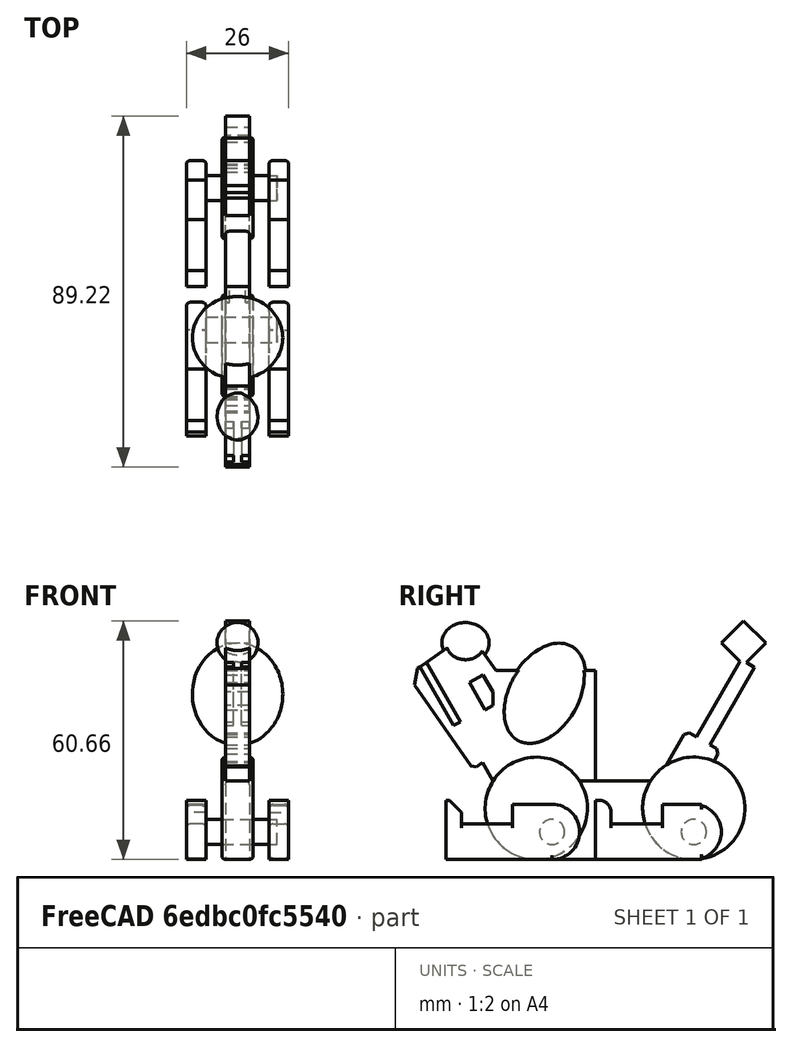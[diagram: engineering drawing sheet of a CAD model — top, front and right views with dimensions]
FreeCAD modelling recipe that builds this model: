
FCSTD DOCUMENT  (FreeCAD 0.18R16117 (Git))
Label: Robo puppy
License: All rights reserved
LicenseURL: http://en.wikipedia.org/wiki/All_rights_reserved
objects: Part::Box×16, Part::Fillet×10, Part::Cylinder×8, Part::MultiFuse×6, Part::Cut×5, Part::Chamfer×4, Part::Mirroring×2, Part::Ellipsoid×2, Part::Plane×1
note: 54 computed .brp shape members not serialized (recipe doc carries the construction recipe); baked Part::Feature solids carry a one-line shape summary decoded from their .brp

FEATURE [Part::Plane] Plane
  AttacherType = Attacher::AttachEngine3D
  Length = 100
  Placement = pos=(-50,-50,0) rot=(0,0,1;0rad)
  Width = 100
FEATURE [Part::Box] Box  label="Cube"
  AttacherType = Attacher::AttachEngine3D
  Height = 20
  Length = 6
  Placement = pos=(-3,-20,0) rot=(0,0,1;0rad)
  Width = 40
FEATURE [Part::Cylinder] Cylinder  label="wheel1"
  Angle = 360
  AttacherType = Attacher::AttachEngine3D
  Height = 8
  Placement = pos=(-4,-20,13) rot=(0,1,0;1.5708rad)
  Radius = 13
FEATURE [Part::Cylinder] Cylinder001  label="wheel2"
  Angle = 360
  AttacherType = Attacher::AttachEngine3D
  Height = 8
  Placement = pos=(-4,20,13) rot=(0,1,0;1.5708rad)
  Radius = 13
FEATURE [Part::Cylinder] Cylinder002  label="wheel003"
  Angle = 360
  AttacherType = Attacher::AttachEngine3D
  Height = 18
  Placement = pos=(-8,-16,7) rot=(0,1,0;1.5708rad)
  Radius = 3.2
FEATURE [Part::Cylinder] Cylinder003  label="wheel004"
  Angle = 360
  AttacherType = Attacher::AttachEngine3D
  Height = 18
  Placement = pos=(-8,20,7) rot=(0,1,0;1.5708rad)
  Radius = 3.2
FEATURE [Part::Cylinder] Cylinder004  label="wheel005"
  Angle = 360
  AttacherType = Attacher::AttachEngine3D
  Height = 18
  Placement = pos=(-8,-16,7) rot=(0,1,0;1.5708rad)
  Radius = 4
FEATURE [Part::Cylinder] Cylinder005  label="wheel006"
  Angle = 360
  AttacherType = Attacher::AttachEngine3D
  Height = 18
  Placement = pos=(-8,20,7) rot=(0,1,0;1.5708rad)
  Radius = 4
FEATURE [Part::Fillet] Fillet
  Base = -> Cylinder
  Edges = 2 edges r=1: [Edge1,Edge3]
FEATURE [Part::Fillet] Fillet001
  Base = -> Box
  Edges = 2 edges r=1: [Edge2,Edge6]
FEATURE [Part::Fillet] Fillet002
  Base = -> Cylinder001
  Edges = 2 edges r=1: [Edge1,Edge3]
FEATURE [Part::MultiFuse] Fusion
  Shapes = -> [Fillet,Fillet002,Fillet001]
FEATURE [Part::Cut] Cut
  Base = -> Fusion
  Tool = -> Cylinder004
FEATURE [Part::Cut] Cut001
  Base = -> Fusion
  Tool = -> Cylinder005
FEATURE [Part::Cylinder] Cylinder006  label="wheel007"
  Angle = 360
  AttacherType = Attacher::AttachEngine3D
  Height = 5
  Placement = pos=(8,-16,7) rot=(0,1,0;1.5708rad)
  Radius = 7
FEATURE [Part::Cylinder] Cylinder007  label="wheel008"
  Angle = 360
  AttacherType = Attacher::AttachEngine3D
  Height = 5
  Placement = pos=(8,20,7) rot=(0,1,0;1.5708rad)
  Radius = 7
FEATURE [Part::Box] Box001  label="Cube001"
  AttacherType = Attacher::AttachEngine3D
  Height = 14
  Length = 5
  Placement = pos=(8,-26,0) rot=(0,0,1;0rad)
  Width = 10
FEATURE [Part::Box] Box002  label="Cube002"
  AttacherType = Attacher::AttachEngine3D
  Height = 14
  Length = 5
  Placement = pos=(8,12,0) rot=(0,0,1;0rad)
  Width = 10
FEATURE [Part::Box] Box003  label="Cube003"
  AttacherType = Attacher::AttachEngine3D
  Height = 9
  Length = 5
  Placement = pos=(8,-39,0) rot=(1,0,0;0rad)
  Width = 13
FEATURE [Part::Box] Box004  label="Cube004"
  AttacherType = Attacher::AttachEngine3D
  Height = 9
  Length = 5
  Placement = pos=(8,-1,0) rot=(0,0,1;0rad)
  Width = 13
FEATURE [Part::Box] Box005  label="Cube005"
  AttacherType = Attacher::AttachEngine3D
  Height = 15
  Length = 5
  Placement = pos=(8,-5,0) rot=(0,0,1;0rad)
  Width = 4
FEATURE [Part::Box] Box006  label="Cube006"
  AttacherType = Attacher::AttachEngine3D
  Height = 15
  Length = 5
  Placement = pos=(8,-43,0) rot=(0,0,1;0rad)
  Width = 4
FEATURE [Part::Fillet] Fillet003
  Base = -> Box005
  Edges = 1 edges r=3: [Edge12]
FEATURE [Part::Chamfer] Chamfer
  Base = -> Box006
  Edges = 1 edges r=3: [Edge12]
FEATURE [Part::Fillet] Fillet004
  Base = -> Box003
  Edges = 2 edges r=1: [Edge2,Edge6]
FEATURE [Part::Fillet] Fillet005
  Base = -> Cylinder006
  Edges = 2 edges r=1: [Edge1,Edge3]
FEATURE [Part::Fillet] Fillet006
  Base = -> Box001
  Edges = 2 edges r=1: [Edge2,Edge6]
FEATURE [Part::Fillet] Fillet007
  Base = -> Box004
  Edges = 2 edges r=1: [Edge2,Edge6]
FEATURE [Part::Fillet] Fillet008
  Base = -> Cylinder007
  Edges = 2 edges r=1: [Edge1,Edge3]
FEATURE [Part::Fillet] Fillet009
  Base = -> Box002
  Edges = 2 edges r=1: [Edge2,Edge6]
FEATURE [Part::MultiFuse] Fusion001
  Shapes = -> [Chamfer,Fillet004,Fillet005,Fillet006]
FEATURE [Part::MultiFuse] Fusion002
  Shapes = -> [Fillet003,Fillet007,Fillet008,Fillet009]
FEATURE [Part::Mirroring] Part__Mirroring  label="Fusion001 (Mirror #1)"
  Base = (0,0,0)
  Normal = (1,0,0)
  Source = -> Fusion001
FEATURE [Part::Mirroring] Part__Mirroring001  label="Fusion002 (Mirror #2)"
  Base = (0,0,0)
  Normal = (1,0,0)
  Source = -> Fusion002
FEATURE [Part::MultiFuse] Fusion003  label="Front legs"
  Shapes = -> [Part__Mirroring,Fusion001]
FEATURE [Part::MultiFuse] Fusion004  label="Back legs"
  Shapes = -> [Part__Mirroring001,Fusion002]
FEATURE [Part::Box] Box007  label="Cube007"
  AttacherType = Attacher::AttachEngine3D
  Height = 8
  Length = 6
  Placement = pos=(-3,-31,20) rot=(1,0,0;0.523599rad)
  Width = 13
FEATURE [Part::Box] Box008  label="Cube008"
  AttacherType = Attacher::AttachEngine3D
  Height = 10
  Length = 6
  Placement = pos=(-3,13,24) rot=(-1,0,0;0.523599rad)
  Width = 10
FEATURE [Part::Box] Box009  label="Cube009"
  AttacherType = Attacher::AttachEngine3D
  Height = 24
  Length = 6
  Placement = pos=(-3,20,30) rot=(-1,0,0;0.523599rad)
  Width = 4
FEATURE [Part::Box] Box010  label="Cube010"
  AttacherType = Attacher::AttachEngine3D
  Height = 8
  Length = 6
  Placement = pos=(-3,27,55) rot=(-1,0,0;0.785398rad)
  Width = 8
FEATURE [Part::Chamfer] Chamfer001
  Base = -> Box008
  Edges = 2 edges r=1: [Edge10,Edge12]
FEATURE [Part::Box] Box011  label="Cube011"
  AttacherType = Attacher::AttachEngine3D
  Height = 29
  Length = 6
  Placement = pos=(-3,-36,23) rot=(1,0,0;0.610865rad)
  Width = 19
FEATURE [Part::Chamfer] Chamfer002
  Base = -> Box011
  Edges = 2 edges r=1: [Edge9,Edge11]
FEATURE [Part::Chamfer] Chamfer003
  Base = -> Chamfer002
  Edges = 2 edges r=3: [Edge9,Edge12]
FEATURE [Part::Box] Box012  label="Cube012"
  AttacherType = Attacher::AttachEngine3D
  Height = 8
  Length = 6
  Placement = pos=(-3,-33,38) rot=(1,0,0;0.523599rad)
  Width = 4
FEATURE [Part::Cut] Cut002
  Base = -> Chamfer003
  Tool = -> Box012
FEATURE [Part::Box] Box013  label="Cube013"
  AttacherType = Attacher::AttachEngine3D
  Height = 18
  Length = 2
  Placement = pos=(1,-41,34) rot=(1,0,0;0.523599rad)
  Width = 2
FEATURE [Part::Box] Box014  label="Cube014"
  AttacherType = Attacher::AttachEngine3D
  Height = 18
  Length = 2
  Placement = pos=(-3,-41,34) rot=(1,0,0;0.523599rad)
  Width = 2
FEATURE [Part::Cut] Cut003
  Base = -> Cut002
  Tool = -> Box013
FEATURE [Part::Cut] Cut004
  Base = -> Cut003
  Tool = -> Box014
FEATURE [Part::Ellipsoid] Ellipsoid
  Angle1 = -90
  Angle2 = 90
  Angle3 = 360
  AttacherType = Attacher::AttachEngine3D
  Placement = pos=(0,-38,55) rot=(0,0,1;0rad)
  Radius1 = 5.2
  Radius2 = 5.2
  Radius3 = 6
FEATURE [Part::Ellipsoid] Ellipsoid001
  Angle1 = -90
  Angle2 = 90
  Angle3 = 360
  AttacherType = Attacher::AttachEngine3D
  Placement = pos=(0,-18,42) rot=(-1,0,0;0.523599rad)
  Radius1 = 14
  Radius2 = 11.5
  Radius3 = 9.1
FEATURE [Part::Box] Box015  label="Cube015"
  AttacherType = Attacher::AttachEngine3D
  Height = 28
  Length = 6
  Placement = pos=(-3,-31,20) rot=(1,0,0;0rad)
  Width = 26
FEATURE [Part::MultiFuse] Fusion005  label="Head and Body"
  Shapes = -> [Cylinder003,Cut,Cut001,Box007,Box009,Box010,Chamfer001,Cut004,Box015,Ellipsoid,Ellipsoid001]
